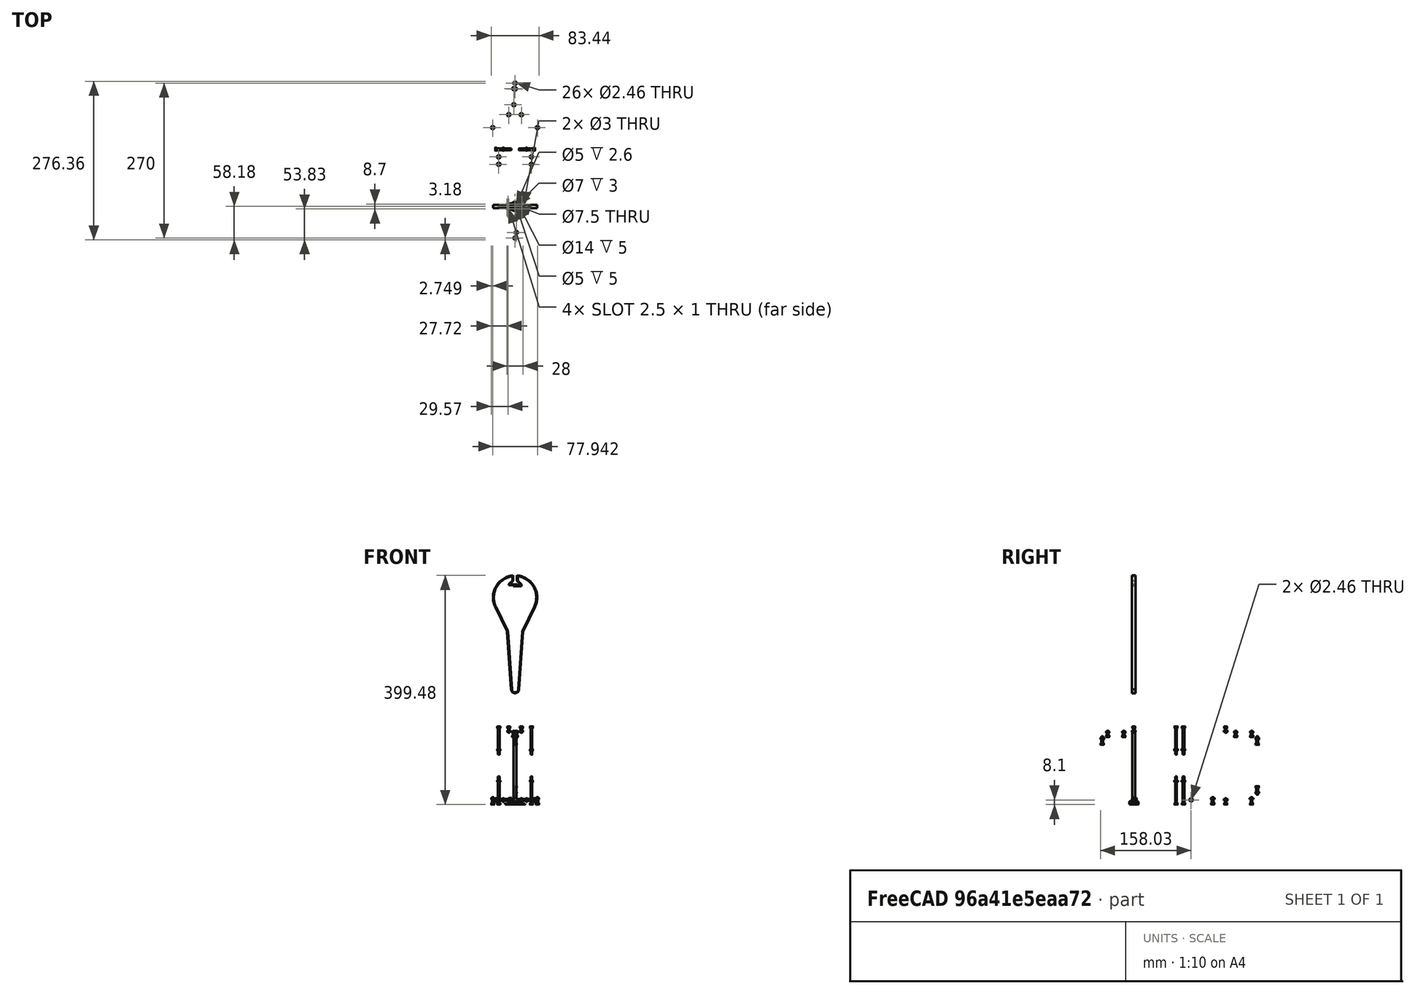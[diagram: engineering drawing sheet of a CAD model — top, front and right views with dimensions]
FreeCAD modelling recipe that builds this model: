
FCSTD DOCUMENT  (FreeCAD 0.19R24276 (Git))
Label: AssemblyArt2
License: All rights reserved
LicenseURL: http://en.wikipedia.org/wiki/All_rights_reserved
objects: Part::FeaturePython×56, App::Link×40, PartDesign::CoordinateSystem×11, App::DocumentObjectGroup×8, App::Part×8, Part::Feature×4, Part::Cylinder×3, PartDesign::Line×2, App::FeaturePython×1
note: 76 computed B-rep shape members (.brp) not serialized (recipe doc carries the construction recipe, not evaluated geometry)
EXTERNAL_REF file=Art2BodyA.FCStd obj=LCS_Art2BodyA
EXTERNAL_REF file=Art2BodyA.FCStd obj=Body001
EXTERNAL_REF file=Art2BodyA.FCStd obj=LCS_Window
EXTERNAL_REF file=Art2BodyAWindow.FCStd obj=LCS_Art2BodyAWindow
EXTERNAL_REF file=Art2BodyAWindow.FCStd obj=Body
EXTERNAL_REF file=Art2BodyA.FCStd obj=LCS_Cover
EXTERNAL_REF file=Art2BodyACover2.FCStd obj=LCS_Art2BodyACover2
EXTERNAL_REF file=Art2BodyACover2.FCStd obj=Body
EXTERNAL_REF file=Art2BodyACover2.FCStd obj=LCS_Union
EXTERNAL_REF file=Art2BodyUnion.FCStd obj=LCS_Art2BodyUnion
EXTERNAL_REF file=Art2BodyUnion.FCStd obj=Body
EXTERNAL_REF file=Art2BodyBCover.FCStd obj=LCS_Union
EXTERNAL_REF file=Art2BodyUnion.FCStd obj=LCS_Art2BodyUnion_1
EXTERNAL_REF file=Art2BodyBCover.FCStd obj=Body
EXTERNAL_REF file=Art2BodyB.FCStd obj=LCS_Art2BodyB
EXTERNAL_REF file=Art2BodyBCover.FCStd obj=LCS_Art2BodyBCover
EXTERNAL_REF file=Art2BodyB.FCStd obj=Body
EXTERNAL_REF file=Art2BodyB.FCStd obj=LCS_BearingFix
EXTERNAL_REF file=CommonBearingFix.FCStd obj=LCS_CommonBearingFix
EXTERNAL_REF file=CommonBearingFix.FCStd obj=Body
EXTERNAL_REF file=Art2BodyB.FCStd obj=LCS_BearingFix001
EXTERNAL_REF file=Art2BodyA.FCStd obj=LCS_BearingFix
EXTERNAL_REF file=Art2BodyAWindow.FCStd obj=LCS_BearingFix
EXTERNAL_REF file=Art2SideCover.FCStd obj=LCS_Art2SideCover
EXTERNAL_REF file=Art2SideCover.FCStd obj=Body
EXTERNAL_REF file=Art2BodyA.FCStd obj=LCS_Tensioner1
EXTERNAL_REF file=Art3TensionerBody.FCStd obj=LCS_Art3TensionerBody
EXTERNAL_REF file=Art3TensionerBody.FCStd obj=Body
EXTERNAL_REF file=Art2BodyA.FCStd obj=LCS_Tensioner001
EXTERNAL_REF file=Art3TensionerBody.FCStd obj=LCS_TopShaft
EXTERNAL_REF file=Art3TensionerPulley.FCStd obj=LCS_Art3TensionerPulley
EXTERNAL_REF file=Art3TensionerPulley.FCStd obj=Body
EXTERNAL_REF file=Art2BodyB.FCStd obj=LCS_Bearing
EXTERNAL_REF file=Art2BodyB.FCStd obj=LCS_Bearing001
EXTERNAL_REF file=Art2BodyA.FCStd obj=LCS_Bearing
EXTERNAL_REF file=Art2BodyAWindow.FCStd obj=LCS_Bearing
EXTERNAL_REF file=Art2BodyB.FCStd obj=LCS_OpticSensor
EXTERNAL_REF file=Art2BodyB.FCStd obj=LCS_OpticSensor1
EXTERNAL_REF file=Art3TensionerPulley.FCStd obj=LCS_Bearing
EXTERNAL_REF file=Art2BodyA.FCStd obj=LCS_Magnet2001
EXTERNAL_REF file=Art2BodyA.FCStd obj=LCS_Magnet1
EXTERNAL_REF file=Art2BodyA.FCStd obj=LCS_Magnet2
EXTERNAL_REF file=Art2BodyB.FCStd obj=LCS_Magnet2
EXTERNAL_REF file=Art2BodyB.FCStd obj=LCS_Magnet1
EXTERNAL_REF file=Art2BodyB.FCStd obj=LCS_Magnet
EXTERNAL_REF file=Art2SideCover.FCStd obj=LCS_Magnet
EXTERNAL_REF file=Art2SideCover.FCStd obj=LCS_Magnet1
EXTERNAL_REF file=Art2SideCover.FCStd obj=LCS_Magnet2
EXTERNAL_REF file=Art2BodyB.FCStd obj=HoleAxis_9
EXTERNAL_REF file=Art2BodyA.FCStd obj=HoleAxis_2
EXTERNAL_REF file=Art2BodyA.FCStd obj=HoleAxis_1
EXTERNAL_REF file=Art2BodyA.FCStd obj=HoleAxis_4
EXTERNAL_REF file=Art2BodyA.FCStd obj=HoleAxis_3
EXTERNAL_REF file=Art2BodyA.FCStd obj=HoleAxis_9
EXTERNAL_REF file=Art2BodyA.FCStd obj=HoleAxis_10
EXTERNAL_REF file=CommonBearingFix.FCStd obj=HoleAxis_1
EXTERNAL_REF file=CommonBearingFix.FCStd obj=HoleAxis_2
EXTERNAL_REF file=Art2BodyAWindow.FCStd obj=HoleAxis_2
EXTERNAL_REF file=Art2BodyAWindow.FCStd obj=HoleAxis_1
EXTERNAL_REF file=Art2BodyAWindow.FCStd obj=HoleAxis_3
EXTERNAL_REF file=Art2BodyAWindow.FCStd obj=HoleAxis_4
EXTERNAL_REF file=Art2BodyAWindow.FCStd obj=HoleAxis_5
EXTERNAL_REF file=Art3TensionerBody.FCStd obj=HoleAxis_1
EXTERNAL_REF file=Art2BodyBCover.FCStd obj=HoleAxis_2
EXTERNAL_REF file=Art2BodyACover2.FCStd obj=HoleAxis_1
EXTERNAL_REF file=Art2BodyA.FCStd obj=HoleAxis_6
EXTERNAL_REF file=Art2BodyA.FCStd obj=HoleAxis_5
EXTERNAL_REF file=Art2BodyA.FCStd obj=HoleAxis_7
EXTERNAL_REF file=Art2BodyA.FCStd obj=HoleAxis_8
EXTERNAL_REF file=Art2BodyB.FCStd obj=HoleAxis_3
EXTERNAL_REF file=Art2BodyB.FCStd obj=HoleAxis_4
EXTERNAL_REF file=Art2BodyB.FCStd obj=HoleAxis_2
EXTERNAL_REF file=Art2BodyB.FCStd obj=HoleAxis_1
EXTERNAL_REF file=Art2BodyUnion.FCStd obj=HoleAxis_7
EXTERNAL_REF file=Art2BodyUnion.FCStd obj=HoleAxis_6
EXTERNAL_REF file=Art2BodyUnion.FCStd obj=HoleAxis_1
EXTERNAL_REF file=Art2BodyUnion.FCStd obj=HoleAxis_2
EXTERNAL_REF file=Art2BodyUnion.FCStd obj=HoleAxis_4
EXTERNAL_REF file=Art2BodyUnion.FCStd obj=HoleAxis_3
EXTERNAL_REF file=Art2BodyUnion.FCStd obj=HoleAxis_5
EXTERNAL_REF file=Art2BodyUnion.FCStd obj=HoleAxis_8
EXTERNAL_REF file=Art2BodyB.FCStd obj=HoleAxis_10
EXTERNAL_REF file=Art2BodyB.FCStd obj=HoleAxis_11
EXTERNAL_REF file=Art2BodyB.FCStd obj=HoleAxis_12
EXTERNAL_REF file=Art2BodyB.FCStd obj=HoleAxis_13
EXTERNAL_REF file=Art2BodyB.FCStd obj=HoleAxis_8
EXTERNAL_REF file=Art2BodyB.FCStd obj=HoleAxis_7
EXTERNAL_REF file=Art2BodyB.FCStd obj=HoleAxis_5
EXTERNAL_REF file=Art2BodyB.FCStd obj=HoleAxis_6
EXTERNAL_REF file=Art2BodyB.FCStd obj=HoleAxis_14
EXTERNAL_REF file=Art2BodyBCover.FCStd obj=HoleAxis_1

FEATURE [PartDesign::CoordinateSystem] LCS_Origin
  AttacherType = Attacher::AttachEngine3D
  MapMode = 2
  Support = -> [X_Axis]
FEATURE [App::DocumentObjectGroup] Constraints
FEATURE [App::FeaturePython] Variables  # WARN: FeaturePython — macro-defined, semantics opaque (R4)
FEATURE [App::Link] Art2BodyA_Art2BodyA
  AssemblyType = Asm4EE
  AttachedBy = #LCS_Art2BodyA
  AttachedTo = Parent Assembly#LCS_Origin
  ElementCount = 0
  LinkTransform = false
  Scale = 1
  ScaleVector = (1,1,1)
  ShowElement = true
  expr: Placement = LCS_Origin.Placement * AttachmentOffset * Art2BodyA#LCS_Art2BodyA.Placement ^ -1
FEATURE [App::Link] Unnamed_Art2BodyAWindow  label="Art2BodyAWindow_Art2BodyAWindow"
  AssemblyType = Asm4EE
  AttachedBy = #LCS_Art2BodyAWindow
  AttachedTo = Art2BodyA_Art2BodyA#LCS_Window
  AttachmentOffset = pos=(0,0,-7) rot=(0.707107,-0.707107,0;3.14159rad)
  ElementCount = 0
  LinkPlacement = pos=(1.45e-14,160,3.64e-14) rot=(0,0,1;0rad)
  LinkTransform = false
  Placement = pos=(1.45e-14,160,3.64e-14) rot=(0,0,1;0rad)
  Scale = 1
  ScaleVector = (1,1,1)
  ShowElement = true
  expr: Placement = Art2BodyA_Art2BodyA.Placement * Art2BodyA#LCS_Window.Placement * AttachmentOffset * Art2BodyAWindow#LCS_Art2BodyAWindow.Placement ^ -1
FEATURE [App::Link] Art2BodyACover2_Art2BodyACover2
  AssemblyType = Asm4EE
  AttachedBy = #LCS_Art2BodyACover2
  AttachedTo = Art2BodyA_Art2BodyA#LCS_Cover
  AttachmentOffset = pos=(0,0,0) rot=(0,0,1;3.14159rad)
  ElementCount = 0
  LinkPlacement = pos=(1.42e-14,-5.68e-14,32) rot=(0,-1,0;3.14159rad)
  LinkTransform = false
  Placement = pos=(1.42e-14,-5.68e-14,32) rot=(0,-1,0;3.14159rad)
  Scale = 1
  ScaleVector = (1,1,1)
  ShowElement = true
  expr: Placement = Art2BodyA_Art2BodyA.Placement * Art2BodyA#LCS_Cover.Placement * AttachmentOffset * Art2BodyACover2#LCS_Art2BodyACover2.Placement ^ -1
FEATURE [App::Link] Art2BodyUnion_Art2BodyUnion
  AssemblyType = Asm4EE
  AttachedBy = #LCS_Art2BodyUnion
  AttachedTo = Art2BodyACover2_Art2BodyACover2#LCS_Union
  AttachmentOffset = pos=(0,0,0) rot=(1,0,0;3.14159rad)
  ElementCount = 0
  LinkPlacement = pos=(-1.48e-14,80,68) rot=(0,0,1;0rad)
  LinkTransform = false
  Placement = pos=(-1.48e-14,80,68) rot=(0,0,1;0rad)
  Scale = 1
  ScaleVector = (1,1,1)
  ShowElement = true
  expr: Placement = Art2BodyACover2_Art2BodyACover2.Placement * Art2BodyACover2#LCS_Union.Placement * AttachmentOffset * Art2BodyUnion#LCS_Art2BodyUnion.Placement ^ -1
FEATURE [App::Link] Art2BodyBCover_Art2BodyBCover
  AssemblyType = Asm4EE
  AttachedBy = #LCS_Union
  AttachedTo = Art2BodyUnion_Art2BodyUnion#LCS_Art2BodyUnion_1
  ElementCount = 0
  LinkPlacement = pos=(2.94e-14,-5.68e-14,104) rot=(0,0,1;0rad)
  LinkTransform = false
  Placement = pos=(2.94e-14,-5.68e-14,104) rot=(0,0,1;0rad)
  Scale = 1
  ScaleVector = (1,1,1)
  ShowElement = true
  expr: Placement = Art2BodyUnion_Art2BodyUnion.Placement * Art2BodyUnion#LCS_Art2BodyUnion_1.Placement * AttachmentOffset * Art2BodyBCover#LCS_Union.Placement ^ -1
FEATURE [App::Link] Art2BodyB_Art2BodyB
  AssemblyType = Asm4EE
  AttachedBy = #LCS_Art2BodyB
  AttachedTo = Art2BodyBCover_Art2BodyBCover#LCS_Art2BodyBCover
  AttachmentOffset = pos=(0,0,-5) rot=(1,0,0;3.14159rad)
  ElementCount = 0
  LinkPlacement = pos=(2.13e-14,-7.44e-14,136) rot=(0,1,0;3.14159rad)
  LinkTransform = false
  Placement = pos=(2.13e-14,-7.44e-14,136) rot=(0,1,0;3.14159rad)
  Scale = 1
  ScaleVector = (1,1,1)
  ShowElement = true
  expr: Placement = Art2BodyBCover_Art2BodyBCover.Placement * Art2BodyBCover#LCS_Art2BodyBCover.Placement * AttachmentOffset * Art2BodyB#LCS_Art2BodyB.Placement ^ -1
FEATURE [App::Link] CommonBearingFix_CommonBearingFix
  AssemblyType = Asm4EE
  AttachedBy = #LCS_CommonBearingFix
  AttachedTo = Art2BodyB_Art2BodyB#LCS_BearingFix
  AttachmentOffset = pos=(0,0,0) rot=(1,0,0;3.14159rad)
  ElementCount = 0
  LinkPlacement = pos=(-1.359e-13,160,132) rot=(0,0,1;0rad)
  LinkTransform = false
  Placement = pos=(-1.359e-13,160,132) rot=(0,0,1;0rad)
  Scale = 1
  ScaleVector = (1,1,1)
  ShowElement = true
  expr: Placement = Art2BodyB_Art2BodyB.Placement * Art2BodyB#LCS_BearingFix.Placement * AttachmentOffset * CommonBearingFix#LCS_CommonBearingFix.Placement ^ -1
FEATURE [App::Link] CommonBearingFix_CommonBearingFix001
  AssemblyType = Asm4EE
  AttachedBy = #LCS_CommonBearingFix
  AttachedTo = Art2BodyB_Art2BodyB#LCS_BearingFix001
  AttachmentOffset = pos=(0,0,0) rot=(1,0,0;3.14159rad)
  ElementCount = 0
  LinkPlacement = pos=(3.7e-15,-7.26e-14,132) rot=(0,0,1;0rad)
  LinkTransform = false
  Placement = pos=(3.7e-15,-7.26e-14,132) rot=(0,0,1;0rad)
  Scale = 1
  ScaleVector = (1,1,1)
  ShowElement = true
  expr: Placement = Art2BodyB_Art2BodyB.Placement * Art2BodyB#LCS_BearingFix001.Placement * AttachmentOffset * CommonBearingFix#LCS_CommonBearingFix.Placement ^ -1
FEATURE [App::Link] CommonBearingFix_CommonBearingFix002
  AssemblyType = Asm4EE
  AttachedBy = #LCS_CommonBearingFix
  AttachedTo = Art2BodyA_Art2BodyA#LCS_BearingFix
  AttachmentOffset = pos=(0,0,0) rot=(1,0,0;3.14159rad)
  ElementCount = 0
  LinkPlacement = pos=(1.86e-14,0,4) rot=(0,1,0;3.14159rad)
  LinkTransform = false
  Placement = pos=(1.86e-14,0,4) rot=(0,1,0;3.14159rad)
  Scale = 1
  ScaleVector = (1,1,1)
  ShowElement = true
  expr: Placement = Art2BodyA_Art2BodyA.Placement * Art2BodyA#LCS_BearingFix.Placement * AttachmentOffset * CommonBearingFix#LCS_CommonBearingFix.Placement ^ -1
FEATURE [App::Link] CommonBearingFix_CommonBearingFix003
  AssemblyType = Asm4EE
  AttachedBy = #LCS_CommonBearingFix
  AttachedTo = Unnamed_Art2BodyAWindow#LCS_BearingFix
  AttachmentOffset = pos=(0,0,0) rot=(1,0,0;3.14159rad)
  ElementCount = 0
  LinkPlacement = pos=(3.37e-14,160,4) rot=(0,-1,0;3.14159rad)
  LinkTransform = false
  Placement = pos=(3.37e-14,160,4) rot=(0,-1,0;3.14159rad)
  Scale = 1
  ScaleVector = (1,1,1)
  ShowElement = true
  expr: Placement = Unnamed_Art2BodyAWindow.Placement * Art2BodyAWindow#LCS_BearingFix.Placement * AttachmentOffset * CommonBearingFix#LCS_CommonBearingFix.Placement ^ -1
FEATURE [Part::Feature] Compound001  label="Bearing 625ZZ"
FEATURE [PartDesign::CoordinateSystem] LCS_0
  AttacherType = Attacher::AttachEngine3D
  MapMode = 2
  Support = -> [X_Axis003]
FEATURE [App::Part] Bearing_625ZZ
  Group = -> [LCS_0,Compound001]
  Origin = -> Origin003
FEATURE [PartDesign::CoordinateSystem] LCS_0007
  AttacherType = Attacher::AttachEngine3D
  MapMode = 2
  Support = -> [X_Axis008]
FEATURE [Part::Feature] Fusion155  label="OptoSwitch002"
FEATURE [PartDesign::CoordinateSystem] LCS_OpticSensor
  AttacherType = Attacher::AttachEngine3D
  MapMode = 45
  Placement = pos=(7.5e-15,-1e-16,0) rot=(0,0,1;1.5708rad)
  Support = -> [Fusion155]
FEATURE [PartDesign::Line] HoleAxis_14
  AttacherType = Attacher::AttachEngineLine
  Length = 4.2272
  MapMode = 19
  Placement = pos=(-14,0,1.5) rot=(0,0,1;0rad)
  ResizeMode = 1
  Support = -> [Fusion155]
FEATURE [PartDesign::Line] HoleAxis_15
  AttacherType = Attacher::AttachEngineLine
  Length = 4.2272
  MapMode = 19
  Placement = pos=(14,0,1.5) rot=(0,0,1;0rad)
  ResizeMode = 1
  Support = -> [Fusion155]
FEATURE [App::Part] OpticSensor
  Group = -> [LCS_0007,Fusion155,LCS_OpticSensor,HoleAxis_14,HoleAxis_15]
  Origin = -> Origin008
FEATURE [App::DocumentObjectGroup] Group001  label="Electronics"
  Group = -> [OpticSensor]
FEATURE [App::Link] Unnamed_Art2SideCover  label="Art2SideCover_Art2SideCover"
  AssemblyType = Asm4EE
  AttachedBy = #LCS_Art2SideCover
  AttachedTo = Parent Assembly#LCS_Origin
  ElementCount = 0
  LinkPlacement = pos=(0,0,-2) rot=(0,0,1;0rad)
  LinkTransform = false
  Placement = pos=(0,0,-2) rot=(0,0,1;0rad)
  Scale = 1
  ScaleVector = (1,1,1)
  ShowElement = true
  expr: Placement = LCS_Origin.Placement * AttachmentOffset * Art2SideCover#LCS_Art2SideCover.Placement ^ -1
FEATURE [App::Link] Unnamed_Art2SideCover001  label="Art2SideCover_Art2SideCover001"
  AssemblyType = Asm4EE
  AttachedBy = #LCS_Art2SideCover
  AttachedTo = Art2BodyB_Art2BodyB#LCS_BearingFix001
  AttachmentOffset = pos=(0,0,-4) rot=(0,0,1;4.71239rad)
  ElementCount = 0
  LinkPlacement = pos=(1.15e-14,-7.55e-14,138) rot=(0,-1,0;3.14159rad)
  LinkTransform = false
  Placement = pos=(1.15e-14,-7.55e-14,138) rot=(0,-1,0;3.14159rad)
  Scale = 1
  ScaleVector = (1,1,1)
  ShowElement = true
  expr: Placement = Art2BodyB_Art2BodyB.Placement * Art2BodyB#LCS_BearingFix001.Placement * AttachmentOffset * Art2SideCover#LCS_Art2SideCover.Placement ^ -1
FEATURE [App::Link] Art3TensionerBody_Art3TensionerBody
  AssemblyType = Asm4EE
  AttachedBy = #LCS_Art3TensionerBody
  AttachedTo = Art2BodyA_Art2BodyA#LCS_Tensioner1
  AttachmentOffset = pos=(-15,0,0) rot=(0,0,1;0rad)
  ElementCount = 0
  LinkPlacement = pos=(10.5,99.85,5) rot=(0,0,1;1.5708rad)
  LinkTransform = false
  Placement = pos=(10.5,99.85,5) rot=(0,0,1;1.5708rad)
  Scale = 1
  ScaleVector = (1,1,1)
  ShowElement = true
  expr: Placement = Art2BodyA_Art2BodyA.Placement * Art2BodyA#LCS_Tensioner1.Placement * AttachmentOffset * Art3TensionerBody#LCS_Art3TensionerBody.Placement ^ -1
FEATURE [App::Link] Art3TensionerBody_Art3TensionerBody001
  AssemblyType = Asm4EE
  AttachedBy = #LCS_Art3TensionerBody
  AttachedTo = Art2BodyA_Art2BodyA#LCS_Tensioner001
  AttachmentOffset = pos=(15,0,0) rot=(0,1,0;3.14159rad)
  ElementCount = 0
  LinkPlacement = pos=(-10.5,99.85,5) rot=(0,0,1;4.71239rad)
  LinkTransform = false
  Placement = pos=(-10.5,99.85,5) rot=(0,0,1;4.71239rad)
  Scale = 1
  ScaleVector = (1,1,1)
  ShowElement = true
  expr: Placement = Art2BodyA_Art2BodyA.Placement * Art2BodyA#LCS_Tensioner001.Placement * AttachmentOffset * Art3TensionerBody#LCS_Art3TensionerBody.Placement ^ -1
FEATURE [App::Link] Art3TensionerPulley_Art3TensionerPulley
  AssemblyType = Asm4EE
  AttachedBy = #LCS_Art3TensionerPulley
  AttachedTo = Art3TensionerBody_Art3TensionerBody#LCS_TopShaft
  AttachmentOffset = pos=(0,0,14.5) rot=(1,0,0;3.14159rad)
  ElementCount = 0
  LinkPlacement = pos=(14.5,99.85,16) rot=(0,0,1;1.5708rad)
  LinkTransform = false
  Placement = pos=(14.5,99.85,16) rot=(0,0,1;1.5708rad)
  Scale = 1
  ScaleVector = (1,1,1)
  ShowElement = true
  expr: Placement = Art3TensionerBody_Art3TensionerBody.Placement * Art3TensionerBody#LCS_TopShaft.Placement * AttachmentOffset * Art3TensionerPulley#LCS_Art3TensionerPulley.Placement ^ -1
FEATURE [App::Link] Art3TensionerPulley_Art3TensionerPulley001
  AssemblyType = Asm4EE
  AttachedBy = #LCS_Art3TensionerPulley
  AttachedTo = Art3TensionerBody_Art3TensionerBody001#LCS_TopShaft
  AttachmentOffset = pos=(0,0,14.5) rot=(1,0,0;3.14159rad)
  ElementCount = 0
  LinkPlacement = pos=(-14.5,99.85,16) rot=(0,0,1;4.71239rad)
  LinkTransform = false
  Placement = pos=(-14.5,99.85,16) rot=(0,0,1;4.71239rad)
  Scale = 1
  ScaleVector = (1,1,1)
  ShowElement = true
  expr: Placement = Art3TensionerBody_Art3TensionerBody001.Placement * Art3TensionerBody#LCS_TopShaft.Placement * AttachmentOffset * Art3TensionerPulley#LCS_Art3TensionerPulley.Placement ^ -1
FEATURE [App::Link] Bearing_625ZZ001
  AssemblyType = Asm4EE
  AttachedBy = #LCS_0
  AttachedTo = Art2BodyB_Art2BodyB#LCS_Bearing
  AttachmentOffset = pos=(0,0,0) rot=(1,0,0;3.14159rad)
  ElementCount = 0
  LinkPlacement = pos=(-1.234e-13,160,127) rot=(0,0,-1;4.71239rad)
  LinkTransform = false
  Placement = pos=(-1.234e-13,160,127) rot=(0,0,-1;4.71239rad)
  Scale = 1
  ScaleVector = (1,1,1)
  ShowElement = true
  expr: Placement = Art2BodyB_Art2BodyB.Placement * Art2BodyB#LCS_Bearing.Placement * AttachmentOffset * LCS_0.Placement ^ -1
FEATURE [App::Link] Bearing_625ZZ002
  AssemblyType = Asm4EE
  AttachedBy = #LCS_0
  AttachedTo = Art2BodyB_Art2BodyB#LCS_Bearing001
  AttachmentOffset = pos=(0,0,0) rot=(1,0,0;3.14159rad)
  ElementCount = 0
  LinkPlacement = pos=(2.24e-14,-6.88e-14,127) rot=(0,0,-1;4.71239rad)
  LinkTransform = false
  Placement = pos=(2.24e-14,-6.88e-14,127) rot=(0,0,-1;4.71239rad)
  Scale = 1
  ScaleVector = (1,1,1)
  ShowElement = true
  expr: Placement = Art2BodyB_Art2BodyB.Placement * Art2BodyB#LCS_Bearing001.Placement * AttachmentOffset * LCS_0.Placement ^ -1
FEATURE [App::Link] Bearing_625ZZ003
  AssemblyType = Asm4EE
  AttachedBy = #LCS_0
  AttachedTo = Art2BodyA_Art2BodyA#LCS_Bearing
  AttachmentOffset = pos=(0,0,0) rot=(1,0,0;3.14159rad)
  ElementCount = 0
  LinkPlacement = pos=(0,0,9) rot=(0.707107,0.707107,0;3.14159rad)
  LinkTransform = false
  Placement = pos=(0,0,9) rot=(0.707107,0.707107,0;3.14159rad)
  Scale = 1
  ScaleVector = (1,1,1)
  ShowElement = true
  expr: Placement = Art2BodyA_Art2BodyA.Placement * Art2BodyA#LCS_Bearing.Placement * AttachmentOffset * LCS_0.Placement ^ -1
FEATURE [App::Link] Bearing_625ZZ004
  AssemblyType = Asm4EE
  AttachedBy = #LCS_0
  AttachedTo = Unnamed_Art2BodyAWindow#LCS_Bearing
  ElementCount = 0
  LinkPlacement = pos=(1.45e-14,160,9) rot=(0.707107,-0.707107,0;3.14159rad)
  LinkTransform = false
  Placement = pos=(1.45e-14,160,9) rot=(0.707107,-0.707107,0;3.14159rad)
  Scale = 1
  ScaleVector = (1,1,1)
  ShowElement = true
  expr: Placement = Unnamed_Art2BodyAWindow.Placement * Art2BodyAWindow#LCS_Bearing.Placement * AttachmentOffset * LCS_0.Placement ^ -1
FEATURE [App::Link] OpticSensor001
  AssemblyType = Asm4EE
  AttachedBy = #LCS_OpticSensor
  AttachedTo = Art2BodyB_Art2BodyB#LCS_OpticSensor
  ElementCount = 0
  LinkPlacement = pos=(2.2,-31.4,122) rot=(-0.707107,0.707107,0;3.14159rad)
  LinkTransform = false
  Placement = pos=(2.2,-31.4,122) rot=(-0.707107,0.707107,0;3.14159rad)
  Scale = 1
  ScaleVector = (1,1,1)
  ShowElement = true
  expr: Placement = Art2BodyB_Art2BodyB.Placement * Art2BodyB#LCS_OpticSensor.Placement * AttachmentOffset * LCS_OpticSensor.Placement ^ -1
FEATURE [App::Link] OpticSensor002
  AssemblyType = Asm4EE
  AttachedBy = #LCS_OpticSensor
  AttachedTo = Art2BodyB_Art2BodyB#LCS_OpticSensor1
  AttachmentOffset = pos=(0,0,0) rot=(0,0,1;3.14159rad)
  ElementCount = 0
  LinkPlacement = pos=(-2.2,191.4,122) rot=(0.707107,0.707107,0;3.14159rad)
  LinkTransform = false
  Placement = pos=(-2.2,191.4,122) rot=(0.707107,0.707107,0;3.14159rad)
  Scale = 1
  ScaleVector = (1,1,1)
  ShowElement = true
  expr: Placement = Art2BodyB_Art2BodyB.Placement * Art2BodyB#LCS_OpticSensor1.Placement * AttachmentOffset * LCS_OpticSensor.Placement ^ -1
FEATURE [PartDesign::CoordinateSystem] LCS_0008  label="LCS"
  AttacherType = Attacher::AttachEngine3D
  MapMode = 2
  Support = -> [X_Axis009]
FEATURE [Part::Cylinder] Cylinder
  Angle = 360
  AttacherType = Attacher::AttachEngine3D
  Height = 14
  MapMode = 0
  Radius = 2
FEATURE [App::Part] _x14mm  label="4x14mm"
  Group = -> [LCS_0008,Cylinder]
  Origin = -> Origin009
FEATURE [Part::Feature] Compound002  label="MF84ZZ"
FEATURE [PartDesign::CoordinateSystem] LCS_0009
  AttacherType = Attacher::AttachEngine3D
  MapMode = 2
  Support = -> [X_Axis010]
FEATURE [App::Part] Bearing_MF84ZZ
  Group = -> [LCS_0009,Compound002]
  Origin = -> Origin010
FEATURE [App::DocumentObjectGroup] Group  label="Bearing"
  Group = -> [Bearing_625ZZ,Bearing_MF84ZZ]
FEATURE [App::Link] _x14mm001  label="4x14mm001"
  AssemblyType = Asm4EE
  AttachedBy = #LCS_0008
  AttachedTo = Art3TensionerBody_Art3TensionerBody#LCS_TopShaft
  ElementCount = 0
  LinkPlacement = pos=(14.5,99.85,10.5) rot=(0,0,1;0rad)
  LinkTransform = false
  Placement = pos=(14.5,99.85,10.5) rot=(0,0,1;0rad)
  Scale = 1
  ScaleVector = (1,1,1)
  ShowElement = true
  expr: Placement = Art3TensionerBody_Art3TensionerBody.Placement * Art3TensionerBody#LCS_TopShaft.Placement * AttachmentOffset * LCS_0008.Placement ^ -1
FEATURE [App::Link] _x14mm002  label="4x14mm002"
  AssemblyType = Asm4EE
  AttachedBy = #LCS_0008
  AttachedTo = Art3TensionerBody_Art3TensionerBody001#LCS_TopShaft
  ElementCount = 0
  LinkPlacement = pos=(-14.5,99.85,10.5) rot=(0,0,1;3.14159rad)
  LinkTransform = false
  Placement = pos=(-14.5,99.85,10.5) rot=(0,0,1;3.14159rad)
  Scale = 1
  ScaleVector = (1,1,1)
  ShowElement = true
  expr: Placement = Art3TensionerBody_Art3TensionerBody001.Placement * Art3TensionerBody#LCS_TopShaft.Placement * AttachmentOffset * LCS_0008.Placement ^ -1
FEATURE [App::Link] Bearing_MF84ZZ001
  AssemblyType = Asm4EE
  AttachedBy = #LCS_0009
  AttachedTo = Art3TensionerPulley_Art3TensionerPulley#LCS_Bearing
  AttachmentOffset = pos=(0,0,0) rot=(1,0,0;3.14159rad)
  ElementCount = 0
  LinkPlacement = pos=(14.5,99.85,16) rot=(0,0,1;0rad)
  LinkTransform = false
  Placement = pos=(14.5,99.85,16) rot=(0,0,1;0rad)
  Scale = 1
  ScaleVector = (1,1,1)
  ShowElement = true
  expr: Placement = Art3TensionerPulley_Art3TensionerPulley.Placement * Art3TensionerPulley#LCS_Bearing.Placement * AttachmentOffset * LCS_0009.Placement ^ -1
FEATURE [App::Link] Bearing_MF84ZZ002
  AssemblyType = Asm4EE
  AttachedBy = #LCS_0009
  AttachedTo = Art3TensionerPulley_Art3TensionerPulley001#LCS_Bearing
  AttachmentOffset = pos=(0,0,0) rot=(1,0,0;3.14159rad)
  ElementCount = 0
  LinkPlacement = pos=(-14.5,99.85,16) rot=(0,0,-1;3.14159rad)
  LinkTransform = false
  Placement = pos=(-14.5,99.85,16) rot=(0,0,-1;3.14159rad)
  Scale = 1
  ScaleVector = (1,1,1)
  ShowElement = true
  expr: Placement = Art3TensionerPulley_Art3TensionerPulley001.Placement * Art3TensionerPulley#LCS_Bearing.Placement * AttachmentOffset * LCS_0009.Placement ^ -1
FEATURE [Part::Cylinder] Cylinder001
  Angle = 360
  AttacherType = Attacher::AttachEngine3D
  Height = 1
  MapMode = 0
  Radius = 4
FEATURE [PartDesign::CoordinateSystem] LCS_0010
  AttacherType = Attacher::AttachEngine3D
  MapMode = 2
  Support = -> [X_Axis011]
FEATURE [App::Part] Magnet
  Group = -> [LCS_0010,Cylinder001]
  Origin = -> Origin011
FEATURE [App::DocumentObjectGroup] Group003  label="Magnets"
  Group = -> [Magnet]
FEATURE [App::Link] Magnet001
  AssemblyType = Asm4EE
  AttachedBy = #LCS_0010
  AttachedTo = Art2BodyA_Art2BodyA#LCS_Magnet2001
  ElementCount = 0
  LinkPlacement = pos=(0,-54.5,1.1) rot=(0.707107,-0.707107,0;3.14159rad)
  LinkTransform = false
  Placement = pos=(0,-54.5,1.1) rot=(0.707107,-0.707107,0;3.14159rad)
  Scale = 1
  ScaleVector = (1,1,1)
  ShowElement = true
  expr: Placement = Art2BodyA_Art2BodyA.Placement * Art2BodyA#LCS_Magnet2001.Placement * AttachmentOffset * LCS_0010.Placement ^ -1
FEATURE [App::Link] Magnet002
  AssemblyType = Asm4EE
  AttachedBy = #LCS_0010
  AttachedTo = Art2BodyA_Art2BodyA#LCS_Magnet1
  ElementCount = 0
  LinkPlacement = pos=(0,80,1.1) rot=(0.707107,-0.707107,0;3.14159rad)
  LinkTransform = false
  Placement = pos=(0,80,1.1) rot=(0.707107,-0.707107,0;3.14159rad)
  Scale = 1
  ScaleVector = (1,1,1)
  ShowElement = true
  expr: Placement = Art2BodyA_Art2BodyA.Placement * Art2BodyA#LCS_Magnet1.Placement * AttachmentOffset * LCS_0010.Placement ^ -1
FEATURE [App::Link] Magnet003
  AssemblyType = Asm4EE
  AttachedBy = #LCS_0010
  AttachedTo = Art2BodyA_Art2BodyA#LCS_Magnet2
  ElementCount = 0
  LinkPlacement = pos=(0,214.5,1.1) rot=(0.707107,-0.707107,0;3.14159rad)
  LinkTransform = false
  Placement = pos=(0,214.5,1.1) rot=(0.707107,-0.707107,0;3.14159rad)
  Scale = 1
  ScaleVector = (1,1,1)
  ShowElement = true
  expr: Placement = Art2BodyA_Art2BodyA.Placement * Art2BodyA#LCS_Magnet2.Placement * AttachmentOffset * LCS_0010.Placement ^ -1
FEATURE [App::Link] Magnet004
  AssemblyType = Asm4EE
  AttachedBy = #LCS_0010
  AttachedTo = Art2BodyB_Art2BodyB#LCS_Magnet2
  ElementCount = 0
  LinkPlacement = pos=(6.5e-14,-54.5,134.9) rot=(0,0,-1;1.5708rad)
  LinkTransform = false
  Placement = pos=(6.5e-14,-54.5,134.9) rot=(0,0,-1;1.5708rad)
  Scale = 1
  ScaleVector = (1,1,1)
  ShowElement = true
  expr: Placement = Art2BodyB_Art2BodyB.Placement * Art2BodyB#LCS_Magnet2.Placement * AttachmentOffset * LCS_0010.Placement ^ -1
FEATURE [App::Link] Magnet005
  AssemblyType = Asm4EE
  AttachedBy = #LCS_0010
  AttachedTo = Art2BodyB_Art2BodyB#LCS_Magnet1
  ElementCount = 0
  LinkPlacement = pos=(-4.26e-14,80,134.9) rot=(0,0,-1;1.5708rad)
  LinkTransform = false
  Placement = pos=(-4.26e-14,80,134.9) rot=(0,0,-1;1.5708rad)
  Scale = 1
  ScaleVector = (1,1,1)
  ShowElement = true
  expr: Placement = Art2BodyB_Art2BodyB.Placement * Art2BodyB#LCS_Magnet1.Placement * AttachmentOffset * LCS_0010.Placement ^ -1
FEATURE [App::Link] Magnet006
  AssemblyType = Asm4EE
  AttachedBy = #LCS_0010
  AttachedTo = Art2BodyB_Art2BodyB#LCS_Magnet
  ElementCount = 0
  LinkPlacement = pos=(-1.502e-13,214.5,134.9) rot=(0,0,-1;1.5708rad)
  LinkTransform = false
  Placement = pos=(-1.502e-13,214.5,134.9) rot=(0,0,-1;1.5708rad)
  Scale = 1
  ScaleVector = (1,1,1)
  ShowElement = true
  expr: Placement = Art2BodyB_Art2BodyB.Placement * Art2BodyB#LCS_Magnet.Placement * AttachmentOffset * LCS_0010.Placement ^ -1
FEATURE [App::Link] Magnet007
  AssemblyType = Asm4EE
  AttachedBy = #LCS_0010
  AttachedTo = Unnamed_Art2SideCover#LCS_Magnet
  ElementCount = 0
  LinkPlacement = pos=(0,-54.5,-1.1) rot=(0,0,1;1.5708rad)
  LinkTransform = false
  Placement = pos=(0,-54.5,-1.1) rot=(0,0,1;1.5708rad)
  Scale = 1
  ScaleVector = (1,1,1)
  ShowElement = true
  expr: Placement = Unnamed_Art2SideCover.Placement * Art2SideCover#LCS_Magnet.Placement * AttachmentOffset * LCS_0010.Placement ^ -1
FEATURE [App::Link] Magnet008
  AssemblyType = Asm4EE
  AttachedBy = #LCS_0010
  AttachedTo = Unnamed_Art2SideCover#LCS_Magnet1
  ElementCount = 0
  LinkPlacement = pos=(0,80,-1.1) rot=(0,0,1;1.5708rad)
  LinkTransform = false
  Placement = pos=(0,80,-1.1) rot=(0,0,1;1.5708rad)
  Scale = 1
  ScaleVector = (1,1,1)
  ShowElement = true
  expr: Placement = Unnamed_Art2SideCover.Placement * Art2SideCover#LCS_Magnet1.Placement * AttachmentOffset * LCS_0010.Placement ^ -1
FEATURE [App::Link] Magnet009
  AssemblyType = Asm4EE
  AttachedBy = #LCS_0010
  AttachedTo = Unnamed_Art2SideCover#LCS_Magnet2
  ElementCount = 0
  LinkPlacement = pos=(0,214.5,-1.1) rot=(0,0,1;1.5708rad)
  LinkTransform = false
  Placement = pos=(0,214.5,-1.1) rot=(0,0,1;1.5708rad)
  Scale = 1
  ScaleVector = (1,1,1)
  ShowElement = true
  expr: Placement = Unnamed_Art2SideCover.Placement * Art2SideCover#LCS_Magnet2.Placement * AttachmentOffset * LCS_0010.Placement ^ -1
FEATURE [App::Link] Magnet010
  AssemblyType = Asm4EE
  AttachedBy = #LCS_0010
  AttachedTo = Unnamed_Art2SideCover001#LCS_Magnet2
  ElementCount = 0
  LinkPlacement = pos=(-1.598e-13,214.5,137.1) rot=(-0.707107,-0.707107,0;3.14159rad)
  LinkTransform = false
  Placement = pos=(-1.598e-13,214.5,137.1) rot=(-0.707107,-0.707107,0;3.14159rad)
  Scale = 1
  ScaleVector = (1,1,1)
  ShowElement = true
  expr: Placement = Unnamed_Art2SideCover001.Placement * Art2SideCover#LCS_Magnet2.Placement * AttachmentOffset * LCS_0010.Placement ^ -1
FEATURE [App::Link] Magnet011
  AssemblyType = Asm4EE
  AttachedBy = #LCS_0010
  AttachedTo = Unnamed_Art2SideCover001#LCS_Magnet1
  ElementCount = 0
  LinkPlacement = pos=(-5.22e-14,80,137.1) rot=(-0.707107,-0.707107,0;3.14159rad)
  LinkTransform = false
  Placement = pos=(-5.22e-14,80,137.1) rot=(-0.707107,-0.707107,0;3.14159rad)
  Scale = 1
  ScaleVector = (1,1,1)
  ShowElement = true
  expr: Placement = Unnamed_Art2SideCover001.Placement * Art2SideCover#LCS_Magnet1.Placement * AttachmentOffset * LCS_0010.Placement ^ -1
FEATURE [App::Link] Magnet012
  AssemblyType = Asm4EE
  AttachedBy = #LCS_0010
  AttachedTo = Unnamed_Art2SideCover001#LCS_Magnet
  ElementCount = 0
  LinkPlacement = pos=(5.54e-14,-54.5,137.1) rot=(-0.707107,-0.707107,0;3.14159rad)
  LinkTransform = false
  Placement = pos=(5.54e-14,-54.5,137.1) rot=(-0.707107,-0.707107,0;3.14159rad)
  Scale = 1
  ScaleVector = (1,1,1)
  ShowElement = true
  expr: Placement = Unnamed_Art2SideCover001.Placement * Art2SideCover#LCS_Magnet.Placement * AttachmentOffset * LCS_0010.Placement ^ -1
FEATURE [Part::FeaturePython] Nut  label="M3-Nut"  # WARN: FeaturePython — macro-defined, semantics opaque (R4)
  AssemblyType = Asm4EE
  AttachedBy = Origin
  AttachedTo = Art2BodyB_Art2BodyB#HoleAxis_9
  AttachmentOffset = pos=(0,0,0) rot=(0.707107,-0.707107,0;3.14159rad)
  Placement = pos=(-11,160,129) rot=(0.707107,0.707107,0;3.14159rad)
  diameter = 4
  invert = false
  matchOuter = false
  offset = 0
  thread = false
  type = 7
  expr: Placement = Art2BodyB_Art2BodyB.Placement * Art2BodyB#HoleAxis_9.Placement * AttachmentOffset
FEATURE [Part::FeaturePython] Nut001  label="M3-Nut070"  # WARN: FeaturePython — macro-defined, semantics opaque (R4)
  AssemblyType = Asm4EE
  AttachedBy = Origin
  AttachedTo = Art2BodyA_Art2BodyA#HoleAxis_2
  AttachmentOffset = pos=(0,0,0) rot=(0.707107,-0.707107,0;3.14159rad)
  Placement = pos=(-6e-15,215,22) rot=(0.707107,-0.707107,0;3.14159rad)
  diameter = 4
  invert = false
  matchOuter = false
  offset = 0
  thread = false
  type = 7
  expr: Placement = Art2BodyA_Art2BodyA.Placement * Art2BodyA#HoleAxis_2.Placement * AttachmentOffset
FEATURE [Part::FeaturePython] Nut002  label="M3-Nut071"  # WARN: FeaturePython — macro-defined, semantics opaque (R4)
  AssemblyType = Asm4EE
  AttachedBy = Origin
  AttachedTo = Art2BodyA_Art2BodyA#HoleAxis_1
  AttachmentOffset = pos=(0,0,0) rot=(-0.707107,0.707107,0;3.14159rad)
  Placement = pos=(-3e-15,205,11.5) rot=(0.707107,-0.707107,0;3.14159rad)
  diameter = 4
  invert = false
  matchOuter = false
  offset = 0
  thread = false
  type = 7
  expr: Placement = Art2BodyA_Art2BodyA.Placement * Art2BodyA#HoleAxis_1.Placement * AttachmentOffset
FEATURE [Part::FeaturePython] Nut003  label="M3-Nut072"  # WARN: FeaturePython — macro-defined, semantics opaque (R4)
  AssemblyType = Asm4EE
  AttachedBy = Origin
  AttachedTo = Art2BodyA_Art2BodyA#HoleAxis_4
  AttachmentOffset = pos=(0,0,0) rot=(0.707107,-0.707107,0;3.14159rad)
  Placement = pos=(38.9711,137.5,11.5) rot=(0.258819,0.965926,0;3.14159rad)
  diameter = 4
  invert = false
  matchOuter = false
  offset = 0
  thread = false
  type = 7
  expr: Placement = Art2BodyA_Art2BodyA.Placement * Art2BodyA#HoleAxis_4.Placement * AttachmentOffset
FEATURE [Part::FeaturePython] Nut004  label="M3-Nut073"  # WARN: FeaturePython — macro-defined, semantics opaque (R4)
  AssemblyType = Asm4EE
  AttachedBy = Origin
  AttachedTo = Art2BodyA_Art2BodyA#HoleAxis_3
  AttachmentOffset = pos=(0,0,0) rot=(0.707107,-0.707107,0;3.14159rad)
  Placement = pos=(-38.9711,137.5,11.5) rot=(0.965926,0.258819,0;3.14159rad)
  diameter = 4
  invert = false
  matchOuter = false
  offset = 0
  thread = false
  type = 7
  expr: Placement = Art2BodyA_Art2BodyA.Placement * Art2BodyA#HoleAxis_3.Placement * AttachmentOffset
FEATURE [Part::FeaturePython] Nut005  label="M3-Nut074"  # WARN: FeaturePython — macro-defined, semantics opaque (R4)
  AssemblyType = Asm4EE
  AttachedBy = Origin
  AttachedTo = Art2BodyA_Art2BodyA#HoleAxis_9
  AttachmentOffset = pos=(0,0,0) rot=(0,0,1;1.5708rad)
  Placement = pos=(11,0,7) rot=(0,0,1;1.5708rad)
  diameter = 4
  invert = false
  matchOuter = false
  offset = 0
  thread = false
  type = 7
  expr: Placement = Art2BodyA_Art2BodyA.Placement * Art2BodyA#HoleAxis_9.Placement * AttachmentOffset
FEATURE [Part::FeaturePython] Nut006  label="M3-Nut075"  # WARN: FeaturePython — macro-defined, semantics opaque (R4)
  AssemblyType = Asm4EE
  AttachedBy = Origin
  AttachedTo = Art2BodyA_Art2BodyA#HoleAxis_10
  AttachmentOffset = pos=(0,0,0) rot=(0,0,1;1.5708rad)
  Placement = pos=(-11,0,7) rot=(0,0,1;1.5708rad)
  diameter = 4
  invert = false
  matchOuter = false
  offset = 0
  thread = false
  type = 7
  expr: Placement = Art2BodyA_Art2BodyA.Placement * Art2BodyA#HoleAxis_10.Placement * AttachmentOffset
FEATURE [Part::FeaturePython] Screw001  label="M3x8-Screw"  # WARN: FeaturePython — macro-defined, semantics opaque (R4)
  AssemblyType = Asm4EE
  AttachedBy = Origin
  AttachedTo = OpticSensor001#HoleAxis_15
  Placement = pos=(2.2,-45.4,120.5) rot=(0.707107,-0.707107,0;3.14159rad)
  diameter = 4
  invert = false
  length = 2
  lengthCustom = 8
  matchOuter = false
  offset = 0
  thread = false
  type = 33
  expr: Placement = OpticSensor001.Placement * HoleAxis_15.Placement * AttachmentOffset
FEATURE [Part::FeaturePython] Screw002  label="M3x8-Screw034"  # WARN: FeaturePython — macro-defined, semantics opaque (R4)
  AssemblyType = Asm4EE
  AttachedBy = Origin
  AttachedTo = CommonBearingFix_CommonBearingFix002#HoleAxis_1
  Placement = pos=(11,-2e-15,3) rot=(0,1,0;3.14159rad)
  diameter = 4
  invert = false
  length = 2
  lengthCustom = 8
  matchOuter = false
  offset = 0
  thread = false
  type = 33
  expr: Placement = CommonBearingFix_CommonBearingFix002.Placement * CommonBearingFix#HoleAxis_1.Placement * AttachmentOffset
FEATURE [Part::FeaturePython] Screw003  label="M3x8-Screw035"  # WARN: FeaturePython — macro-defined, semantics opaque (R4)
  AssemblyType = Asm4EE
  AttachedBy = Origin
  AttachedTo = CommonBearingFix_CommonBearingFix002#HoleAxis_2
  Placement = pos=(-11,2e-15,3) rot=(0,1,0;3.14159rad)
  diameter = 4
  invert = false
  length = 2
  lengthCustom = 8
  matchOuter = false
  offset = 0
  thread = false
  type = 33
  expr: Placement = CommonBearingFix_CommonBearingFix002.Placement * CommonBearingFix#HoleAxis_2.Placement * AttachmentOffset
FEATURE [Part::FeaturePython] Screw004  label="M3x8-Screw037"  # WARN: FeaturePython — macro-defined, semantics opaque (R4)
  AssemblyType = Asm4EE
  AttachedBy = Origin
  AttachedTo = CommonBearingFix_CommonBearingFix003#HoleAxis_2
  Placement = pos=(-11,160,3) rot=(0,1,0;3.14159rad)
  diameter = 4
  invert = false
  length = 2
  lengthCustom = 8
  matchOuter = false
  offset = 0
  thread = false
  type = 33
  expr: Placement = CommonBearingFix_CommonBearingFix003.Placement * CommonBearingFix#HoleAxis_2.Placement * AttachmentOffset
FEATURE [Part::FeaturePython] Screw005  label="M3x8-Screw036"  # WARN: FeaturePython — macro-defined, semantics opaque (R4)
  AssemblyType = Asm4EE
  AttachedBy = Origin
  AttachedTo = CommonBearingFix_CommonBearingFix003#HoleAxis_1
  Placement = pos=(11,160,3) rot=(0,1,0;3.14159rad)
  diameter = 4
  invert = false
  length = 2
  lengthCustom = 8
  matchOuter = false
  offset = 0
  thread = false
  type = 33
  expr: Placement = CommonBearingFix_CommonBearingFix003.Placement * CommonBearingFix#HoleAxis_1.Placement * AttachmentOffset
FEATURE [Part::FeaturePython] Screw006  label="M3x10-Screw"  # WARN: FeaturePython — macro-defined, semantics opaque (R4)
  AssemblyType = Asm4EE
  AttachedBy = Origin
  AttachedTo = Unnamed_Art2BodyAWindow#HoleAxis_2
  AttachmentOffset = pos=(0,0,0) rot=(1,0,0;3.14159rad)
  Placement = pos=(-38.9711,137.5,3) rot=(0.866025,-0.5,0;3.14159rad)
  diameter = 4
  invert = false
  length = 3
  lengthCustom = 10
  matchOuter = false
  offset = 0
  thread = false
  type = 33
  expr: Placement = Unnamed_Art2BodyAWindow.Placement * Art2BodyAWindow#HoleAxis_2.Placement * AttachmentOffset
FEATURE [Part::FeaturePython] Screw007  label="M3x10-Screw010"  # WARN: FeaturePython — macro-defined, semantics opaque (R4)
  AssemblyType = Asm4EE
  AttachedBy = Origin
  AttachedTo = Unnamed_Art2BodyAWindow#HoleAxis_1
  AttachmentOffset = pos=(0,0,0) rot=(1,0,0;3.14159rad)
  Placement = pos=(1.5e-14,205,3) rot=(0,1,0;3.14159rad)
  diameter = 4
  invert = false
  length = 3
  lengthCustom = 10
  matchOuter = false
  offset = 0
  thread = false
  type = 33
  expr: Placement = Unnamed_Art2BodyAWindow.Placement * Art2BodyAWindow#HoleAxis_1.Placement * AttachmentOffset
FEATURE [Part::FeaturePython] Screw008  label="M3x10-Screw011"  # WARN: FeaturePython — macro-defined, semantics opaque (R4)
  AssemblyType = Asm4EE
  AttachedBy = Origin
  AttachedTo = Unnamed_Art2BodyAWindow#HoleAxis_3
  AttachmentOffset = pos=(0,0,0) rot=(1,0,0;3.14159rad)
  Placement = pos=(38.9711,137.5,3) rot=(0.866025,0.5,0;3.14159rad)
  diameter = 4
  invert = false
  length = 3
  lengthCustom = 10
  matchOuter = false
  offset = 0
  thread = false
  type = 33
  expr: Placement = Unnamed_Art2BodyAWindow.Placement * Art2BodyAWindow#HoleAxis_3.Placement * AttachmentOffset
FEATURE [Part::FeaturePython] Nut007  label="M3-Nut077"  # WARN: FeaturePython — macro-defined, semantics opaque (R4)
  AssemblyType = Asm4EE
  AttachedBy = Origin
  AttachedTo = Unnamed_Art2BodyAWindow#HoleAxis_4
  AttachmentOffset = pos=(0,0,0) rot=(0.707107,-0.707107,0;3.14159rad)
  Placement = pos=(11,160,7) rot=(0,0,1;1.5708rad)
  diameter = 4
  invert = false
  matchOuter = false
  offset = 0
  thread = false
  type = 7
  expr: Placement = Unnamed_Art2BodyAWindow.Placement * Art2BodyAWindow#HoleAxis_4.Placement * AttachmentOffset
FEATURE [Part::FeaturePython] Nut008  label="M3-Nut076"  # WARN: FeaturePython — macro-defined, semantics opaque (R4)
  AssemblyType = Asm4EE
  AttachedBy = Origin
  AttachedTo = Unnamed_Art2BodyAWindow#HoleAxis_5
  AttachmentOffset = pos=(0,0,0) rot=(0.707107,-0.707107,0;3.14159rad)
  Placement = pos=(-11,160,7) rot=(0,0,1;1.5708rad)
  diameter = 4
  invert = false
  matchOuter = false
  offset = 0
  thread = false
  type = 7
  expr: Placement = Unnamed_Art2BodyAWindow.Placement * Art2BodyAWindow#HoleAxis_5.Placement * AttachmentOffset
FEATURE [Part::FeaturePython] Nut009  label="M3-Nut079"  # WARN: FeaturePython — macro-defined, semantics opaque (R4)
  AssemblyType = Asm4EE
  AttachedBy = Origin
  AttachedTo = Art3TensionerBody_Art3TensionerBody#HoleAxis_1
  AttachmentOffset = pos=(0,0,0) rot=(0,0,-1;4.71239rad)
  Placement = pos=(21.65,99.85,8) rot=(0.707107,0,-0.707107;3.14159rad)
  diameter = 4
  invert = false
  matchOuter = false
  offset = 0
  thread = false
  type = 7
  expr: Placement = Art3TensionerBody_Art3TensionerBody.Placement * Art3TensionerBody#HoleAxis_1.Placement * AttachmentOffset
FEATURE [Part::FeaturePython] Nut010  label="M3-Nut078"  # WARN: FeaturePython — macro-defined, semantics opaque (R4)
  AssemblyType = Asm4EE
  AttachedBy = Origin
  AttachedTo = Art3TensionerBody_Art3TensionerBody001#HoleAxis_1
  AttachmentOffset = pos=(0,0,0) rot=(0,0,1;1.5708rad)
  Placement = pos=(-21.65,99.85,8) rot=(0,1,0;1.5708rad)
  diameter = 4
  invert = false
  matchOuter = false
  offset = 0
  thread = false
  type = 7
  expr: Placement = Art3TensionerBody_Art3TensionerBody001.Placement * Art3TensionerBody#HoleAxis_1.Placement * AttachmentOffset
FEATURE [Part::FeaturePython] Screw009  label="M3x25-Screw"  # WARN: FeaturePython — macro-defined, semantics opaque (R4)
  AssemblyType = Asm4EE
  AttachedBy = Origin
  AttachedTo = Art3TensionerBody_Art3TensionerBody#HoleAxis_1
  AttachmentOffset = pos=(0,0,-10) rot=(1,0,0;3.14159rad)
  Placement = pos=(31.65,99.85,8) rot=(0.57735,0.57735,0.57735;2.0944rad)
  diameter = 4
  invert = false
  length = 8
  lengthCustom = 25
  matchOuter = false
  offset = 0
  thread = false
  type = 33
  expr: Placement = Art3TensionerBody_Art3TensionerBody.Placement * Art3TensionerBody#HoleAxis_1.Placement * AttachmentOffset
FEATURE [Part::FeaturePython] Screw010  label="M3x25-Screw001"  # WARN: FeaturePython — macro-defined, semantics opaque (R4)
  AssemblyType = Asm4EE
  AttachedBy = Origin
  AttachedTo = Art3TensionerBody_Art3TensionerBody001#HoleAxis_1
  AttachmentOffset = pos=(0,0,-10) rot=(1,0,0;3.14159rad)
  Placement = pos=(-31.65,99.85,8) rot=(-0.57735,0.57735,0.57735;4.18879rad)
  diameter = 4
  invert = false
  length = 8
  lengthCustom = 25
  matchOuter = false
  offset = 0
  thread = false
  type = 33
  expr: Placement = Art3TensionerBody_Art3TensionerBody001.Placement * Art3TensionerBody#HoleAxis_1.Placement * AttachmentOffset
FEATURE [Part::FeaturePython] Screw011  label="M3x12-Screw"  # WARN: FeaturePython — macro-defined, semantics opaque (R4)
  AssemblyType = Asm4EE
  AttachedBy = Origin
  AttachedTo = Art2BodyBCover_Art2BodyBCover#HoleAxis_2
  AttachmentOffset = pos=(0,0,0) rot=(1,0,0;3.14159rad)
  Placement = pos=(6e-14,-55,107) rot=(1,0,0;3.14159rad)
  diameter = 4
  invert = false
  length = 4
  lengthCustom = 12
  matchOuter = false
  offset = 0
  thread = false
  type = 33
  expr: Placement = Art2BodyBCover_Art2BodyBCover.Placement * Art2BodyBCover#HoleAxis_2.Placement * AttachmentOffset
FEATURE [Part::FeaturePython] Screw012  label="M3x12-Screw003"  # WARN: FeaturePython — macro-defined, semantics opaque (R4)
  AssemblyType = Asm4EE
  AttachedBy = Origin
  AttachedTo = Art2BodyACover2_Art2BodyACover2#HoleAxis_1
  AttachmentOffset = pos=(0,0,0) rot=(1,0,0;3.14159rad)
  Placement = pos=(-3.4e-14,215,29) rot=(0,0,1;3.14159rad)
  diameter = 4
  invert = false
  length = 4
  lengthCustom = 12
  matchOuter = false
  offset = 0
  thread = false
  type = 33
  expr: Placement = Art2BodyACover2_Art2BodyACover2.Placement * Art2BodyACover2#HoleAxis_1.Placement * AttachmentOffset
FEATURE [Part::FeaturePython] Screw013  label="M3x46-Screw"  # WARN: FeaturePython — macro-defined, semantics opaque (R4)
  AssemblyType = Asm4EE
  AttachedBy = Origin
  AttachedTo = Art2BodyA_Art2BodyA#HoleAxis_6
  Placement = pos=(-28.5,73.5,2.9) rot=(1,0,0;3.14159rad)
  diameter = 4
  invert = false
  length = 10
  lengthCustom = 46
  matchOuter = false
  offset = 0
  thread = false
  type = 33
  expr: Placement = Art2BodyA_Art2BodyA.Placement * Art2BodyA#HoleAxis_6.Placement * AttachmentOffset
FEATURE [Part::FeaturePython] Screw014  label="M3x46-Screw019"  # WARN: FeaturePython — macro-defined, semantics opaque (R4)
  AssemblyType = Asm4EE
  AttachedBy = Origin
  AttachedTo = Art2BodyA_Art2BodyA#HoleAxis_5
  Placement = pos=(-28.5,86.5,2.9) rot=(1,0,0;3.14159rad)
  diameter = 4
  invert = false
  length = 10
  lengthCustom = 46
  matchOuter = false
  offset = 0
  thread = false
  type = 33
  expr: Placement = Art2BodyA_Art2BodyA.Placement * Art2BodyA#HoleAxis_5.Placement * AttachmentOffset
FEATURE [Part::FeaturePython] Screw015  label="M3x46-Screw020"  # WARN: FeaturePython — macro-defined, semantics opaque (R4)
  AssemblyType = Asm4EE
  AttachedBy = Origin
  AttachedTo = Art2BodyA_Art2BodyA#HoleAxis_7
  Placement = pos=(28.5,73.5,2.9) rot=(1,0,0;3.14159rad)
  diameter = 4
  invert = false
  length = 10
  lengthCustom = 46
  matchOuter = false
  offset = 0
  thread = false
  type = 33
  expr: Placement = Art2BodyA_Art2BodyA.Placement * Art2BodyA#HoleAxis_7.Placement * AttachmentOffset
FEATURE [Part::FeaturePython] Screw016  label="M3x46-Screw021"  # WARN: FeaturePython — macro-defined, semantics opaque (R4)
  AssemblyType = Asm4EE
  AttachedBy = Origin
  AttachedTo = Art2BodyA_Art2BodyA#HoleAxis_8
  Placement = pos=(28.5,86.5,2.9) rot=(1,0,0;3.14159rad)
  diameter = 4
  invert = false
  length = 10
  lengthCustom = 46
  matchOuter = false
  offset = 0
  thread = false
  type = 33
  expr: Placement = Art2BodyA_Art2BodyA.Placement * Art2BodyA#HoleAxis_8.Placement * AttachmentOffset
FEATURE [Part::FeaturePython] Screw017  label="M3x46-Screw022"  # WARN: FeaturePython — macro-defined, semantics opaque (R4)
  AssemblyType = Asm4EE
  AttachedBy = Origin
  AttachedTo = Art2BodyB_Art2BodyB#HoleAxis_3
  AttachmentOffset = pos=(0,0,0) rot=(1,0,0;3.14159rad)
  Placement = pos=(28.5,73.5,133.1) rot=(0,0,1;3.14159rad)
  diameter = 4
  invert = false
  length = 10
  lengthCustom = 46
  matchOuter = false
  offset = 0
  thread = false
  type = 33
  expr: Placement = Art2BodyB_Art2BodyB.Placement * Art2BodyB#HoleAxis_3.Placement * AttachmentOffset
FEATURE [Part::FeaturePython] Screw018  label="M3x46-Screw023"  # WARN: FeaturePython — macro-defined, semantics opaque (R4)
  AssemblyType = Asm4EE
  AttachedBy = Origin
  AttachedTo = Art2BodyB_Art2BodyB#HoleAxis_4
  AttachmentOffset = pos=(0,0,0) rot=(1,0,0;3.14159rad)
  Placement = pos=(28.5,86.5,133.1) rot=(0,0,1;3.14159rad)
  diameter = 4
  invert = false
  length = 10
  lengthCustom = 46
  matchOuter = false
  offset = 0
  thread = false
  type = 33
  expr: Placement = Art2BodyB_Art2BodyB.Placement * Art2BodyB#HoleAxis_4.Placement * AttachmentOffset
FEATURE [Part::FeaturePython] Screw019  label="M3x46-Screw024"  # WARN: FeaturePython — macro-defined, semantics opaque (R4)
  AssemblyType = Asm4EE
  AttachedBy = Origin
  AttachedTo = Art2BodyB_Art2BodyB#HoleAxis_2
  AttachmentOffset = pos=(0,0,0) rot=(1,0,0;3.14159rad)
  Placement = pos=(-28.5,86.5,133.1) rot=(0,0,1;3.14159rad)
  diameter = 4
  invert = false
  length = 10
  lengthCustom = 46
  matchOuter = false
  offset = 0
  thread = false
  type = 33
  expr: Placement = Art2BodyB_Art2BodyB.Placement * Art2BodyB#HoleAxis_2.Placement * AttachmentOffset
FEATURE [Part::FeaturePython] Screw020  label="M3x46-Screw025"  # WARN: FeaturePython — macro-defined, semantics opaque (R4)
  AssemblyType = Asm4EE
  AttachedBy = Origin
  AttachedTo = Art2BodyB_Art2BodyB#HoleAxis_1
  AttachmentOffset = pos=(0,0,0) rot=(1,0,0;3.14159rad)
  Placement = pos=(-28.5,73.5,133.1) rot=(0,0,1;3.14159rad)
  diameter = 4
  invert = false
  length = 10
  lengthCustom = 46
  matchOuter = false
  offset = 0
  thread = false
  type = 33
  expr: Placement = Art2BodyB_Art2BodyB.Placement * Art2BodyB#HoleAxis_1.Placement * AttachmentOffset
FEATURE [Part::FeaturePython] Nut011  label="M3-Nut080"  # WARN: FeaturePython — macro-defined, semantics opaque (R4)
  AssemblyType = Asm4EE
  AttachedBy = Origin
  AttachedTo = Art2BodyUnion_Art2BodyUnion#HoleAxis_7
  AttachmentOffset = pos=(0,0,0) rot=(0.707107,-0.707107,0;3.14159rad)
  Placement = pos=(-28.5,86.5,39.5) rot=(0,0,-1;1.5708rad)
  diameter = 4
  invert = false
  matchOuter = false
  offset = 0
  thread = false
  type = 7
  expr: Placement = Art2BodyUnion_Art2BodyUnion.Placement * Art2BodyUnion#HoleAxis_7.Placement * AttachmentOffset
FEATURE [Part::FeaturePython] Nut012  label="M3-Nut081"  # WARN: FeaturePython — macro-defined, semantics opaque (R4)
  AssemblyType = Asm4EE
  AttachedBy = Origin
  AttachedTo = Art2BodyUnion_Art2BodyUnion#HoleAxis_6
  AttachmentOffset = pos=(0,0,0) rot=(0.707107,-0.707107,0;3.14159rad)
  Placement = pos=(28.5,86.5,39.5) rot=(0,0,1;1.5708rad)
  diameter = 4
  invert = false
  matchOuter = false
  offset = 0
  thread = false
  type = 7
  expr: Placement = Art2BodyUnion_Art2BodyUnion.Placement * Art2BodyUnion#HoleAxis_6.Placement * AttachmentOffset
FEATURE [Part::FeaturePython] Nut013  label="M3-Nut082"  # WARN: FeaturePython — macro-defined, semantics opaque (R4)
  AssemblyType = Asm4EE
  AttachedBy = Origin
  AttachedTo = Art2BodyUnion_Art2BodyUnion#HoleAxis_1
  AttachmentOffset = pos=(0,0,0) rot=(0.707107,-0.707107,0;3.14159rad)
  Placement = pos=(-28.5,73.5,39.5) rot=(0,0,-1;1.5708rad)
  diameter = 4
  invert = false
  matchOuter = false
  offset = 0
  thread = false
  type = 7
  expr: Placement = Art2BodyUnion_Art2BodyUnion.Placement * Art2BodyUnion#HoleAxis_1.Placement * AttachmentOffset
FEATURE [Part::FeaturePython] Nut014  label="M3-Nut083"  # WARN: FeaturePython — macro-defined, semantics opaque (R4)
  AssemblyType = Asm4EE
  AttachedBy = Origin
  AttachedTo = Art2BodyUnion_Art2BodyUnion#HoleAxis_2
  AttachmentOffset = pos=(0,0,0) rot=(0.707107,-0.707107,0;3.14159rad)
  Placement = pos=(28.5,73.5,39.5) rot=(0,0,1;1.5708rad)
  diameter = 4
  invert = false
  matchOuter = false
  offset = 0
  thread = false
  type = 7
  expr: Placement = Art2BodyUnion_Art2BodyUnion.Placement * Art2BodyUnion#HoleAxis_2.Placement * AttachmentOffset
FEATURE [Part::FeaturePython] Nut015  label="M3-Nut084"  # WARN: FeaturePython — macro-defined, semantics opaque (R4)
  AssemblyType = Asm4EE
  AttachedBy = Origin
  AttachedTo = Art2BodyUnion_Art2BodyUnion#HoleAxis_4
  AttachmentOffset = pos=(0,0,0) rot=(0.707107,-0.707107,0;3.14159rad)
  Placement = pos=(-28.5,73.5,96.5) rot=(0.707107,0.707107,0;3.14159rad)
  diameter = 4
  invert = false
  matchOuter = false
  offset = 0
  thread = false
  type = 7
  expr: Placement = Art2BodyUnion_Art2BodyUnion.Placement * Art2BodyUnion#HoleAxis_4.Placement * AttachmentOffset
FEATURE [Part::FeaturePython] Nut016  label="M3-Nut085"  # WARN: FeaturePython — macro-defined, semantics opaque (R4)
  AssemblyType = Asm4EE
  AttachedBy = Origin
  AttachedTo = Art2BodyUnion_Art2BodyUnion#HoleAxis_3
  AttachmentOffset = pos=(0,0,0) rot=(0.707107,-0.707107,0;3.14159rad)
  Placement = pos=(28.5,73.5,96.5) rot=(0.707107,-0.707107,0;3.14159rad)
  diameter = 4
  invert = false
  matchOuter = false
  offset = 0
  thread = false
  type = 7
  expr: Placement = Art2BodyUnion_Art2BodyUnion.Placement * Art2BodyUnion#HoleAxis_3.Placement * AttachmentOffset
FEATURE [Part::FeaturePython] Nut017  label="M3-Nut086"  # WARN: FeaturePython — macro-defined, semantics opaque (R4)
  AssemblyType = Asm4EE
  AttachedBy = Origin
  AttachedTo = Art2BodyUnion_Art2BodyUnion#HoleAxis_5
  AttachmentOffset = pos=(0,0,0) rot=(-0.707107,-0.707107,0;3.14159rad)
  Placement = pos=(28.5,86.5,96.5) rot=(0.707107,0.707107,0;3.14159rad)
  diameter = 4
  invert = false
  matchOuter = false
  offset = 0
  thread = false
  type = 7
  expr: Placement = Art2BodyUnion_Art2BodyUnion.Placement * Art2BodyUnion#HoleAxis_5.Placement * AttachmentOffset
FEATURE [Part::FeaturePython] Nut018  label="M3-Nut087"  # WARN: FeaturePython — macro-defined, semantics opaque (R4)
  AssemblyType = Asm4EE
  AttachedBy = Origin
  AttachedTo = Art2BodyUnion_Art2BodyUnion#HoleAxis_8
  AttachmentOffset = pos=(0,0,0) rot=(0.707107,-0.707107,0;3.14159rad)
  Placement = pos=(-28.5,86.5,96.5) rot=(0.707107,0.707107,0;3.14159rad)
  diameter = 4
  invert = false
  matchOuter = false
  offset = 0
  thread = false
  type = 7
  expr: Placement = Art2BodyUnion_Art2BodyUnion.Placement * Art2BodyUnion#HoleAxis_8.Placement * AttachmentOffset
FEATURE [Part::FeaturePython] Screw021  label="M3x8-Screw038"  # WARN: FeaturePython — macro-defined, semantics opaque (R4)
  AssemblyType = Asm4EE
  AttachedBy = Origin
  AttachedTo = CommonBearingFix_CommonBearingFix001#HoleAxis_1
  Placement = pos=(-11,-8.2e-14,133) rot=(0,0,1;0rad)
  diameter = 4
  invert = false
  length = 2
  lengthCustom = 8
  matchOuter = false
  offset = 0
  thread = false
  type = 33
  expr: Placement = CommonBearingFix_CommonBearingFix001.Placement * CommonBearingFix#HoleAxis_1.Placement * AttachmentOffset
FEATURE [Part::FeaturePython] Screw022  label="M3x8-Screw039"  # WARN: FeaturePython — macro-defined, semantics opaque (R4)
  AssemblyType = Asm4EE
  AttachedBy = Origin
  AttachedTo = CommonBearingFix_CommonBearingFix001#HoleAxis_2
  Placement = pos=(11,-6.5e-14,133) rot=(0,0,1;0rad)
  diameter = 4
  invert = false
  length = 2
  lengthCustom = 8
  matchOuter = false
  offset = 0
  thread = false
  type = 33
  expr: Placement = CommonBearingFix_CommonBearingFix001.Placement * CommonBearingFix#HoleAxis_2.Placement * AttachmentOffset
FEATURE [Part::FeaturePython] Screw023  label="M3x8-Screw040"  # WARN: FeaturePython — macro-defined, semantics opaque (R4)
  AssemblyType = Asm4EE
  AttachedBy = Origin
  AttachedTo = CommonBearingFix_CommonBearingFix#HoleAxis_2
  Placement = pos=(11,160,133) rot=(0,0,1;0rad)
  diameter = 4
  invert = false
  length = 2
  lengthCustom = 8
  matchOuter = false
  offset = 0
  thread = false
  type = 33
  expr: Placement = CommonBearingFix_CommonBearingFix.Placement * CommonBearingFix#HoleAxis_2.Placement * AttachmentOffset
FEATURE [Part::FeaturePython] Screw024  label="M3x8-Screw041"  # WARN: FeaturePython — macro-defined, semantics opaque (R4)
  AssemblyType = Asm4EE
  AttachedBy = Origin
  AttachedTo = CommonBearingFix_CommonBearingFix#HoleAxis_1
  Placement = pos=(-11,160,133) rot=(0,0,1;0rad)
  diameter = 4
  invert = false
  length = 2
  lengthCustom = 8
  matchOuter = false
  offset = 0
  thread = false
  type = 33
  expr: Placement = CommonBearingFix_CommonBearingFix.Placement * CommonBearingFix#HoleAxis_1.Placement * AttachmentOffset
FEATURE [Part::FeaturePython] Nut019  label="M3-Nut088"  # WARN: FeaturePython — macro-defined, semantics opaque (R4)
  AssemblyType = Asm4EE
  AttachedBy = Origin
  AttachedTo = Art2BodyB_Art2BodyB#HoleAxis_10
  AttachmentOffset = pos=(0,0,0) rot=(-0.707107,-0.707107,0;3.14159rad)
  Placement = pos=(11,160,129) rot=(0.707107,-0.707107,0;3.14159rad)
  diameter = 4
  invert = false
  matchOuter = false
  offset = 0
  thread = false
  type = 7
  expr: Placement = Art2BodyB_Art2BodyB.Placement * Art2BodyB#HoleAxis_10.Placement * AttachmentOffset
FEATURE [Part::FeaturePython] Nut020  label="M3-Nut089"  # WARN: FeaturePython — macro-defined, semantics opaque (R4)
  AssemblyType = Asm4EE
  AttachedBy = Origin
  AttachedTo = Art2BodyB_Art2BodyB#HoleAxis_11
  Placement = pos=(-2.2,177.4,125) rot=(0,0,1;0rad)
  diameter = 4
  invert = false
  matchOuter = false
  offset = 0
  thread = false
  type = 7
  expr: Placement = Art2BodyB_Art2BodyB.Placement * Art2BodyB#HoleAxis_11.Placement * AttachmentOffset
FEATURE [Part::FeaturePython] Nut021  label="M3-Nut090"  # WARN: FeaturePython — macro-defined, semantics opaque (R4)
  AssemblyType = Asm4EE
  AttachedBy = Origin
  AttachedTo = Art2BodyB_Art2BodyB#HoleAxis_12
  Placement = pos=(-2.2,205.4,125) rot=(0,0,1;0rad)
  diameter = 4
  invert = false
  matchOuter = false
  offset = 0
  thread = false
  type = 7
  expr: Placement = Art2BodyB_Art2BodyB.Placement * Art2BodyB#HoleAxis_12.Placement * AttachmentOffset
FEATURE [Part::FeaturePython] Nut022  label="M3-Nut091"  # WARN: FeaturePython — macro-defined, semantics opaque (R4)
  AssemblyType = Asm4EE
  AttachedBy = Origin
  AttachedTo = Art2BodyB_Art2BodyB#HoleAxis_13
  AttachmentOffset = pos=(0,0,0) rot=(0.707107,-0.707107,0;3.14159rad)
  Placement = pos=(-1.7e-13,215,114) rot=(0,0,-1;1.5708rad)
  diameter = 4
  invert = false
  matchOuter = false
  offset = 0
  thread = false
  type = 7
  expr: Placement = Art2BodyB_Art2BodyB.Placement * Art2BodyB#HoleAxis_13.Placement * AttachmentOffset
FEATURE [Part::FeaturePython] Nut023  label="M3-Nut092"  # WARN: FeaturePython — macro-defined, semantics opaque (R4)
  AssemblyType = Asm4EE
  AttachedBy = Origin
  AttachedTo = Art2BodyB_Art2BodyB#HoleAxis_8
  AttachmentOffset = pos=(0,0,0) rot=(0.707107,-0.707107,0;3.14159rad)
  Placement = pos=(-11,-8e-14,129) rot=(0.707107,0.707107,0;3.14159rad)
  diameter = 4
  invert = false
  matchOuter = false
  offset = 0
  thread = false
  type = 7
  expr: Placement = Art2BodyB_Art2BodyB.Placement * Art2BodyB#HoleAxis_8.Placement * AttachmentOffset
FEATURE [Part::FeaturePython] Nut024  label="M3-Nut093"  # WARN: FeaturePython — macro-defined, semantics opaque (R4)
  AssemblyType = Asm4EE
  AttachedBy = Origin
  AttachedTo = Art2BodyB_Art2BodyB#HoleAxis_7
  AttachmentOffset = pos=(0,0,0) rot=(0.707107,-0.707107,0;3.14159rad)
  Placement = pos=(11,-6.2e-14,129) rot=(0.707107,0.707107,0;3.14159rad)
  diameter = 4
  invert = false
  matchOuter = false
  offset = 0
  thread = false
  type = 7
  expr: Placement = Art2BodyB_Art2BodyB.Placement * Art2BodyB#HoleAxis_7.Placement * AttachmentOffset
FEATURE [Part::FeaturePython] Nut025  label="M3-Nut094"  # WARN: FeaturePython — macro-defined, semantics opaque (R4)
  AssemblyType = Asm4EE
  AttachedBy = Origin
  AttachedTo = Art2BodyB_Art2BodyB#HoleAxis_5
  AttachmentOffset = pos=(0,0,0) rot=(-0.707107,0.707107,0;3.14159rad)
  Placement = pos=(7e-14,-55,114) rot=(0,0,-1;1.5708rad)
  diameter = 4
  invert = false
  matchOuter = false
  offset = 0
  thread = false
  type = 7
  expr: Placement = Art2BodyB_Art2BodyB.Placement * Art2BodyB#HoleAxis_5.Placement * AttachmentOffset
FEATURE [Part::FeaturePython] Nut026  label="M3-Nut095"  # WARN: FeaturePython — macro-defined, semantics opaque (R4)
  AssemblyType = Asm4EE
  AttachedBy = Origin
  AttachedTo = Art2BodyB_Art2BodyB#HoleAxis_6
  Placement = pos=(2.2,-17.4,125) rot=(0,0,1;3.14159rad)
  diameter = 4
  invert = false
  matchOuter = false
  offset = 0
  thread = false
  type = 7
  expr: Placement = Art2BodyB_Art2BodyB.Placement * Art2BodyB#HoleAxis_6.Placement * AttachmentOffset
FEATURE [Part::FeaturePython] Nut027  label="M3-Nut096"  # WARN: FeaturePython — macro-defined, semantics opaque (R4)
  AssemblyType = Asm4EE
  AttachedBy = Origin
  AttachedTo = Art2BodyB_Art2BodyB#HoleAxis_14
  Placement = pos=(2.2,-45.4,125) rot=(0,0,1;3.14159rad)
  diameter = 4
  invert = false
  matchOuter = false
  offset = 0
  thread = false
  type = 7
  expr: Placement = Art2BodyB_Art2BodyB.Placement * Art2BodyB#HoleAxis_14.Placement * AttachmentOffset
FEATURE [Part::FeaturePython] Screw025  label="M3x8-Screw057"  # WARN: FeaturePython — macro-defined, semantics opaque (R4)
  AssemblyType = Asm4EE
  AttachedBy = Origin
  AttachedTo = OpticSensor001#HoleAxis_14
  Placement = pos=(2.2,-17.4,120.5) rot=(0.707107,-0.707107,0;3.14159rad)
  diameter = 4
  invert = false
  length = 2
  lengthCustom = 8
  matchOuter = false
  offset = 0
  thread = false
  type = 33
  expr: Placement = OpticSensor001.Placement * HoleAxis_14.Placement * AttachmentOffset
FEATURE [Part::FeaturePython] Screw026  label="M3x8-Screw059"  # WARN: FeaturePython — macro-defined, semantics opaque (R4)
  AssemblyType = Asm4EE
  AttachedBy = Origin
  AttachedTo = OpticSensor002#HoleAxis_14
  Placement = pos=(-2.2,177.4,120.5) rot=(0.707107,0.707107,0;3.14159rad)
  diameter = 4
  invert = false
  length = 2
  lengthCustom = 8
  matchOuter = false
  offset = 0
  thread = false
  type = 33
  expr: Placement = OpticSensor002.Placement * HoleAxis_14.Placement * AttachmentOffset
FEATURE [Part::FeaturePython] Screw027  label="M3x8-Screw058"  # WARN: FeaturePython — macro-defined, semantics opaque (R4)
  AssemblyType = Asm4EE
  AttachedBy = Origin
  AttachedTo = OpticSensor002#HoleAxis_15
  Placement = pos=(-2.2,205.4,120.5) rot=(0.707107,0.707107,0;3.14159rad)
  diameter = 4
  invert = false
  length = 2
  lengthCustom = 8
  matchOuter = false
  offset = 0
  thread = false
  type = 33
  expr: Placement = OpticSensor002.Placement * HoleAxis_15.Placement * AttachmentOffset
FEATURE [Part::FeaturePython] Screw028  label="M3x12-Screw004"  # WARN: FeaturePython — macro-defined, semantics opaque (R4)
  AssemblyType = Asm4EE
  AttachedBy = Origin
  AttachedTo = Art2BodyBCover_Art2BodyBCover#HoleAxis_1
  AttachmentOffset = pos=(0,0,0) rot=(1,0,0;3.14159rad)
  Placement = pos=(-9e-14,215,107) rot=(1,0,0;3.14159rad)
  diameter = 4
  invert = false
  length = 4
  lengthCustom = 12
  matchOuter = false
  offset = 0
  thread = false
  type = 33
  expr: Placement = Art2BodyBCover_Art2BodyBCover.Placement * Art2BodyBCover#HoleAxis_1.Placement * AttachmentOffset
FEATURE [App::DocumentObjectGroup] Group004  label="Fasteners"
  Group = -> [Nut001,Nut002,Nut003,Nut004,Nut005,Nut006,Screw002,Screw003,Screw005,Screw004,Screw006,Screw007,Screw008,Nut008,Nut007,Screw010,Nut010,Nut009,Screw009,Screw013,Screw014,Screw015,Screw016,Screw012,Nut011,Nut012,Nut013,Nut014,Nut015,Nut016,Nut017,Nut018,Screw017,Screw018,Screw019,Screw020,Screw021,Screw022,Screw023,Screw024,Nut019,Nut020,Nut021,Nut022,Nut023,Nut024,Nut025,Nut026,Nut027,Nut,Screw001,]
FEATURE [PartDesign::CoordinateSystem] LCS_0011
  AttacherType = Attacher::AttachEngine3D
  MapMode = 2
  Support = -> [X_Axis012]
FEATURE [Part::Cylinder] Cylinder002
  Angle = 360
  AttacherType = Attacher::AttachEngine3D
  Height = 128
  MapMode = 0
  Radius = 2.5
FEATURE [App::Part] _x128mm  label="5x128mm"
  Group = -> [LCS_0011,Cylinder002]
  Origin = -> Origin012
FEATURE [App::DocumentObjectGroup] Group002  label="Shafts"
  Group = -> [_x14mm,_x128mm]
FEATURE [App::Link] _x128mm001  label="5x128mm001"
  AssemblyType = Asm4EE
  AttachedBy = #LCS_0011
  AttachedTo = Bearing_625ZZ004#LCS_0
  AttachmentOffset = pos=(0,0,5) rot=(1,0,0;3.14159rad)
  ElementCount = 0
  LinkPlacement = pos=(1.45e-14,160,4) rot=(0,0,1;4.71239rad)
  LinkTransform = false
  Placement = pos=(1.45e-14,160,4) rot=(0,0,1;4.71239rad)
  Scale = 1
  ScaleVector = (1,1,1)
  ShowElement = true
  expr: Placement = Bearing_625ZZ004.Placement * LCS_0.Placement * AttachmentOffset * LCS_0011.Placement ^ -1
FEATURE [PartDesign::CoordinateSystem] LCS_Art1
  AttacherType = Attacher::AttachEngine3D
  MapMode = 0
  Placement = pos=(0,0,68) rot=(0,0,1;0rad)
FEATURE [PartDesign::CoordinateSystem] LCS_Model_1  label="LCS_Art3"
  AttacherType = Attacher::AttachEngine3D
  MapMode = 0
  Placement = pos=(0,160,68) rot=(0,0,1;0rad)
FEATURE [Part::Feature] Fusion154001  label="GT2Belt001"
FEATURE [PartDesign::CoordinateSystem] LCS_GT2_Belt
  AttacherType = Attacher::AttachEngine3D
  MapMode = 11
  Placement = pos=(0,-3,201) rot=(1,0,0;1.5708rad)
  Support = -> [Fusion154001]
FEATURE [App::Part] GT2_Belt_Art3
  Group = -> [Fusion154001,LCS_GT2_Belt]
  Origin = -> Origin013
FEATURE [App::DocumentObjectGroup] Group005  label="Belts"
  Group = -> [GT2_Belt_Art3]
FEATURE [App::DocumentObjectGroup] Parts
  Group = -> [Group,Group001,Group002,Group003,Group005]
FEATURE [App::Link] GT2_Belt_Art3001
  AssemblyType = Asm4EE
  AttachedBy = #LCS_GT2_Belt
  AttachedTo = Art2BodyA_Art2BodyA#LCS_Art2BodyA
  AttachmentOffset = pos=(0,0,20) rot=(0,-1,0;3.14159rad)
  ElementCount = 0
  LinkPlacement = pos=(-1.23e-14,-201,23) rot=(0,-0.707107,-0.707107;3.14159rad)
  LinkTransform = false
  Placement = pos=(-1.23e-14,-201,23) rot=(0,-0.707107,-0.707107;3.14159rad)
  Scale = 1
  ScaleVector = (1,1,1)
  ShowElement = true
  expr: Placement = Art2BodyA_Art2BodyA.Placement * Art2BodyA#LCS_Art2BodyA.Placement * AttachmentOffset * LCS_GT2_Belt.Placement ^ -1
FEATURE [App::Part] Model
  Configuration = 0
  Group = -> [LCS_Origin,Constraints,Variables,Art2BodyA_Art2BodyA,Unnamed_Art2BodyAWindow,Art2BodyACover2_Art2BodyACover2,Art2BodyUnion_Art2BodyUnion,Art2BodyBCover_Art2BodyBCover,Art2BodyB_Art2BodyB,CommonBearingFix_CommonBearingFix,CommonBearingFix_CommonBearingFix001,CommonBearingFix_CommonBearingFix002,CommonBearingFix_CommonBearingFix003,Unnamed_Art2SideCover,Unnamed_Art2SideCover001,Art3TensionerBody_Art]
  Origin = -> Origin
  Type = Assembly4 Model
